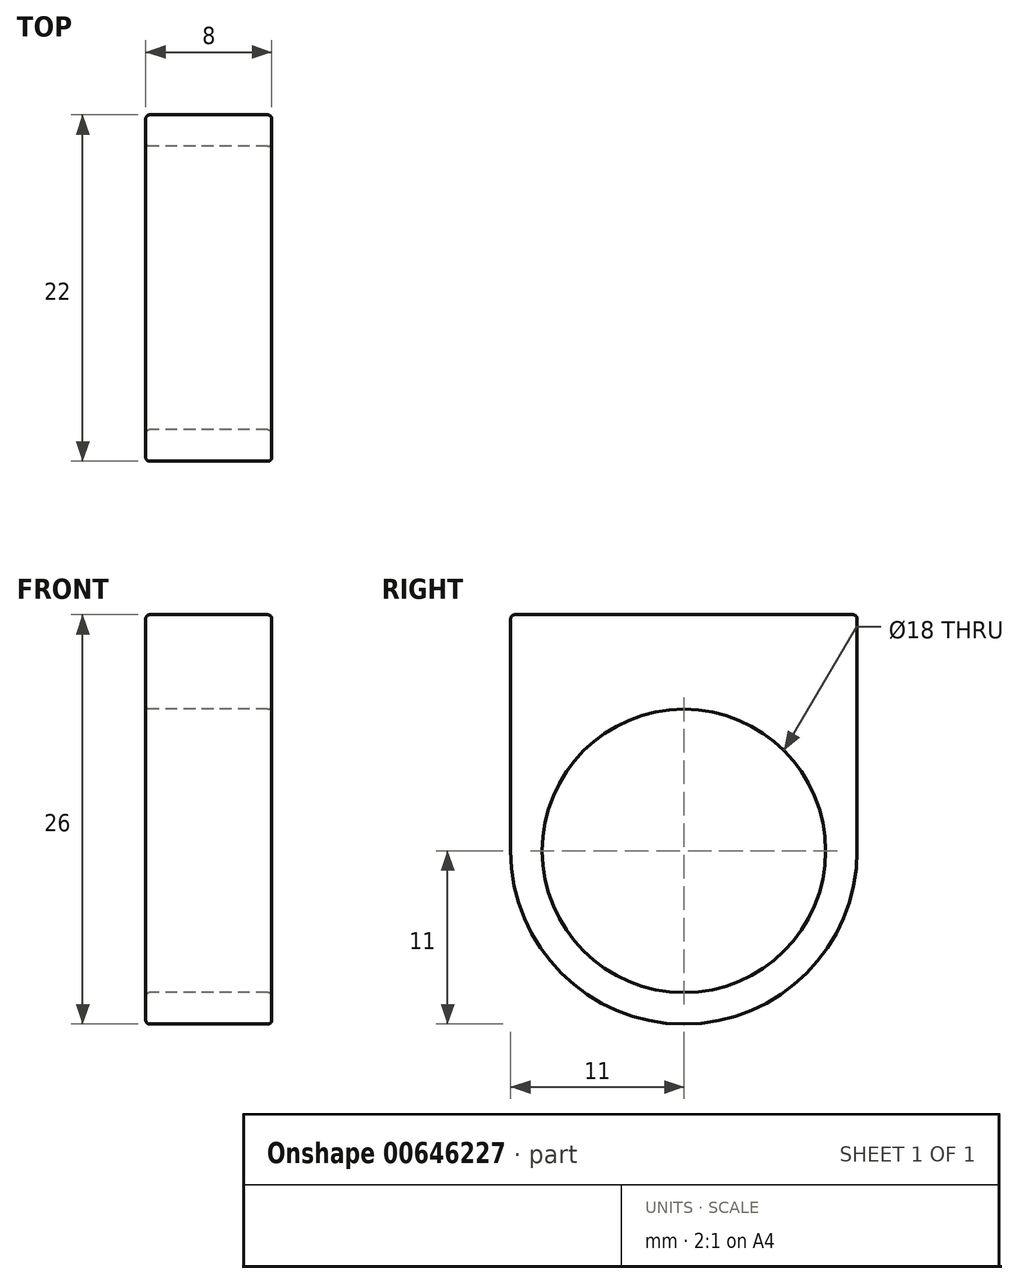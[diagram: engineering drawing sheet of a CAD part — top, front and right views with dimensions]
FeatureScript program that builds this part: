
annotation { "Feature Type Name" : "Feature", "Feature Type Description" : "" }
export const myFeature = defineFeature(function(context is Context, id is Id, definition is map)
    precondition{}
    {
        {
            var Q0;
            Q0=qCreatedBy(makeId("Right.planeOp"),FACE);
            var sketch = newSketch(context, id + "F0", { "sketchPlane" : qUnion([Q0])});
            skCircle(sketch, "E0", {"center": v(0, 0) * mm, "radius": 9 * mm});
            skArc(sketch, "E1", {"start": v(-11, 0) * mm, "mid": v(0, -11) * mm, "end": v(11, 0) * mm});
            skLineSegment(sketch, "E2", {"start": v(-11, 0) * mm, "end": v(-11, 15) * mm});
            skLineSegment(sketch, "E3", {"start": v(11, 0) * mm, "end": v(11, 15) * mm});
            skLineSegment(sketch, "E4", {"start": v(-11, 15) * mm, "end": v(11, 15) * mm});
            skSolve(sketch);
        }
        {
            var Q0;
            Q0 = qSketchRegion(id + "F0", true);
            extrude(context, id + "F1", {"entities" : qUnion([Q0]), "depth" : 8 * mm, "offsetDistance" : 25 * mm});
        }
        {
            var Q0;
            Q0=makeQuery(id+"F1.opExtrude","SWEPT_FACE",FACE,{"disambiguationData":[OSD([sQuery(id+"F0.wireOp",EDGE,"E2")])]});
            var Q1;
            Q1=makeQuery(id+"F1.opExtrude","SWEPT_FACE",FACE,{"disambiguationData":[OSD([sQuery(id+"F0.wireOp",EDGE,"E4")])]});
            var Q2;
            Q2=makeQuery(id+"F1.opExtrude","SWEPT_EDGE",EDGE,{"disambiguationData":[OSD([sQuery(id+"F0.wireOp",EDGE,"E3"),sQuery(id+"F0.wireOp",EDGE,"E4")])]});
            var Q3;
            Q3=makeQuery(id+"F1.opExtrude","SWEPT_FACE",FACE,{"disambiguationData":[OSD([sQuery(id+"F0.wireOp",EDGE,"E1")])]});
            var Q4;
            Q4=makeQuery(id+"F1.opExtrude","SWEPT_FACE",FACE,{"disambiguationData":[OSD([sQuery(id+"F0.wireOp",EDGE,"E0")])]});
            var Q5;
            Q5=makeQuery(id+"F1.opExtrude","CAP_FACE",FACE,{"disambiguationData":[OSD([sQuery(id+"F0.wireOp",EDGE,"E0"),sQuery(id+"F0.wireOp",EDGE,"E1"),sQuery(id+"F0.wireOp",EDGE,"E2"),sQuery(id+"F0.wireOp",EDGE,"E3"),sQuery(id+"F0.wireOp",EDGE,"E4")])],"isStart":true});
            var Q6;
            Q6=makeQuery(id+"F1.opExtrude","CAP_EDGE",EDGE,{"disambiguationData":[OSD([sQuery(id+"F0.wireOp",EDGE,"E4")])],"isStart":true});
            var Q7;
            Q7=makeQuery(id+"F1.opExtrude","CAP_EDGE",EDGE,{"disambiguationData":[OSD([sQuery(id+"F0.wireOp",EDGE,"E4")])],"isStart":false});
            var Q8;
            Q8=makeQuery(id+"F1.opExtrude","CAP_EDGE",EDGE,{"disambiguationData":[OSD([sQuery(id+"F0.wireOp",EDGE,"E1")])],"isStart":false});
            var Q9;
            Q9=makeQuery(id+"F1.opExtrude","SWEPT_FACE",FACE,{"disambiguationData":[OSD([sQuery(id+"F0.wireOp",EDGE,"E3")])]});
            var Q10;
            Q10=makeQuery(id+"F1.opExtrude","CAP_FACE",FACE,{"disambiguationData":[OSD([sQuery(id+"F0.wireOp",EDGE,"E0"),sQuery(id+"F0.wireOp",EDGE,"E1"),sQuery(id+"F0.wireOp",EDGE,"E2"),sQuery(id+"F0.wireOp",EDGE,"E3"),sQuery(id+"F0.wireOp",EDGE,"E4")])],"isStart":false});
            var Q11;
            Q11=makeQuery(id+"F1.opExtrude","CAP_EDGE",EDGE,{"disambiguationData":[OSD([sQuery(id+"F0.wireOp",EDGE,"E1")])],"isStart":true});
            var Q12;
            Q12=makeQuery(id+"F1.opExtrude","SWEPT_EDGE",EDGE,{"disambiguationData":[OSD([sQuery(id+"F0.wireOp",EDGE,"E1"),sQuery(id+"F0.wireOp",EDGE,"E2")])]});
            var Q13;
            Q13=makeQuery(id+"F1.opExtrude","SWEPT_EDGE",EDGE,{"disambiguationData":[OSD([sQuery(id+"F0.wireOp",EDGE,"E2"),sQuery(id+"F0.wireOp",EDGE,"E4")])]});
            var Q14;
            Q14=makeQuery(id+"F1.opExtrude","CAP_EDGE",EDGE,{"disambiguationData":[OSD([sQuery(id+"F0.wireOp",EDGE,"E0")])],"isStart":false});
            var Q15;
            Q15=makeQuery(id+"F1.opExtrude","CAP_EDGE",EDGE,{"disambiguationData":[OSD([sQuery(id+"F0.wireOp",EDGE,"E2")])],"isStart":true});
            var Q16;
            Q16=makeQuery(id+"F1.opExtrude","CAP_EDGE",EDGE,{"disambiguationData":[OSD([sQuery(id+"F0.wireOp",EDGE,"E3")])],"isStart":true});
            var Q17;
            Q17=makeQuery(id+"F1.opExtrude","SWEPT_EDGE",EDGE,{"disambiguationData":[OSD([sQuery(id+"F0.wireOp",EDGE,"E1"),sQuery(id+"F0.wireOp",EDGE,"E3")])]});
            var Q18;
            Q18=makeQuery(id+"F1.opExtrude","CAP_EDGE",EDGE,{"disambiguationData":[OSD([sQuery(id+"F0.wireOp",EDGE,"E2")])],"isStart":false});
            var Q19;
            Q19=makeQuery(id+"F1.opExtrude","CAP_EDGE",EDGE,{"disambiguationData":[OSD([sQuery(id+"F0.wireOp",EDGE,"E3")])],"isStart":false});
            var Q20;
            Q20=makeQuery(id+"F1.opExtrude","CAP_EDGE",EDGE,{"disambiguationData":[OSD([sQuery(id+"F0.wireOp",EDGE,"E0")])],"isStart":true});
            fillet(context, id + "F2", {"entities" : qUnion([Q0, Q1, Q2, Q3, Q4, Q5, Q6, Q7, Q8, Q9, Q10, Q11, Q12, Q13, Q14, Q15, Q16, Q17, Q18, Q19, Q20]), "radius" : 0.25 * mm, "tangentPropagation" : true, "allowEdgeOverflow" : false});
        }
    });
